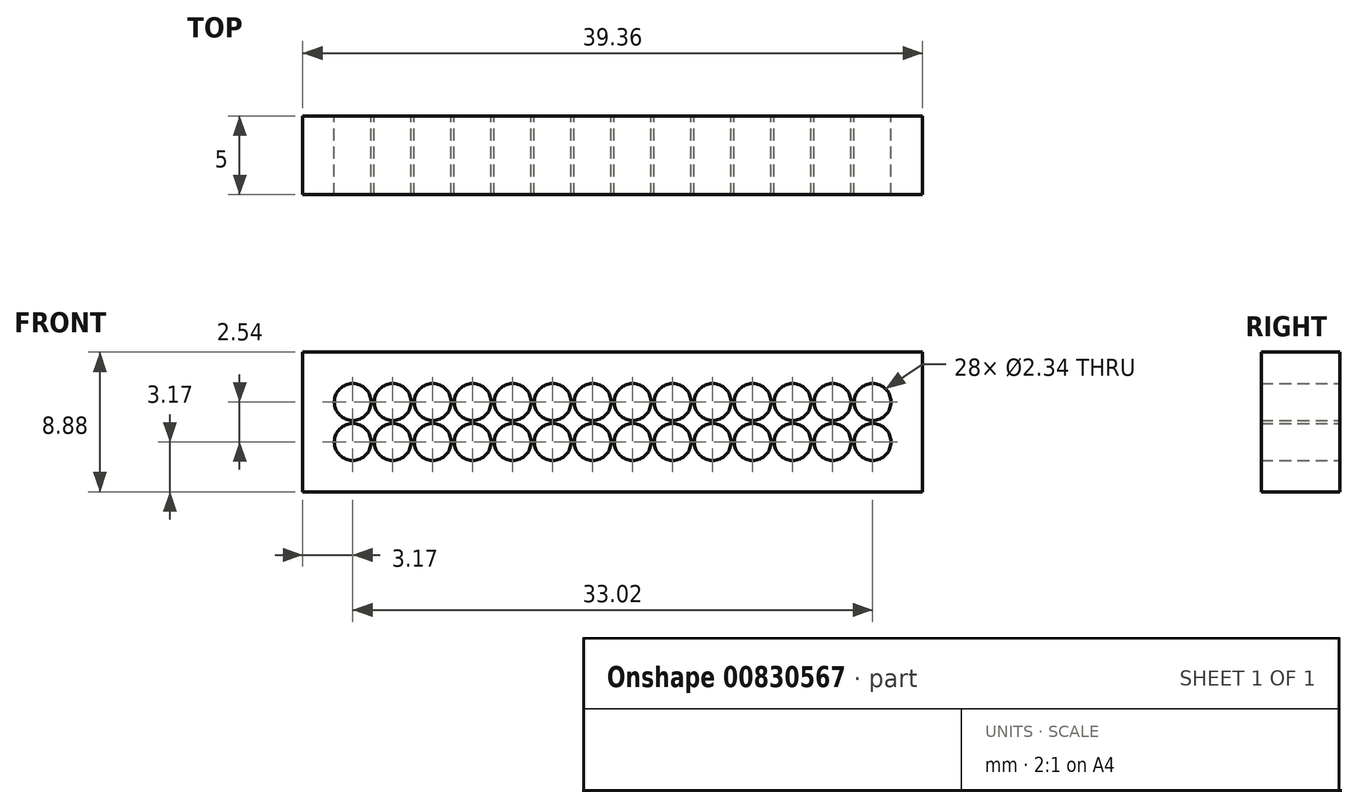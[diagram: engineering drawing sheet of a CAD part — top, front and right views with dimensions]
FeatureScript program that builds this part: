
annotation { "Feature Type Name" : "Feature", "Feature Type Description" : "" }
export const myFeature = defineFeature(function(context is Context, id is Id, definition is map)
    precondition{}
    {
        {
            var Q0;
            Q0=qCreatedBy(makeId("Front.planeOp"),FACE);
            var sketch = newSketch(context, id + "F0", { "sketchPlane" : qUnion([Q0])});
            skCircle(sketch, "E0", {"center": v(-1.27, 1.27) * mm, "radius": 1.17 * mm});
            skCircle(sketch, "E1", {"center": v(1.27, 1.27) * mm, "radius": 1.17 * mm});
            skCircle(sketch, "E2", {"center": v(-1.27, -1.27) * mm, "radius": 1.17 * mm});
            skCircle(sketch, "E3", {"center": v(1.27, -1.27) * mm, "radius": 1.17 * mm});
            skCircle(sketch, "E4", {"center": v(3.8, 1.27) * mm, "radius": 1.17 * mm});
            skCircle(sketch, "E5", {"center": v(6.35, 1.27) * mm, "radius": 1.17 * mm});
            skCircle(sketch, "E6", {"center": v(8.9, 1.27) * mm, "radius": 1.17 * mm});
            skCircle(sketch, "E7", {"center": v(11.43, 1.27) * mm, "radius": 1.17 * mm});
            skCircle(sketch, "E8", {"center": v(13.97, 1.27) * mm, "radius": 1.17 * mm});
            skCircle(sketch, "E9", {"center": v(16.51, 1.27) * mm, "radius": 1.17 * mm});
            skCircle(sketch, "E10", {"center": v(3.8, -1.27) * mm, "radius": 1.17 * mm});
            skCircle(sketch, "E11", {"center": v(6.35, -1.27) * mm, "radius": 1.17 * mm});
            skCircle(sketch, "E12", {"center": v(8.9, -1.27) * mm, "radius": 1.17 * mm});
            skCircle(sketch, "E13", {"center": v(11.43, -1.27) * mm, "radius": 1.17 * mm});
            skCircle(sketch, "E14", {"center": v(13.97, -1.27) * mm, "radius": 1.17 * mm});
            skCircle(sketch, "E15", {"center": v(16.51, -1.27) * mm, "radius": 1.17 * mm});
            skCircle(sketch, "E16", {"center": v(-3.8, 1.27) * mm, "radius": 1.17 * mm});
            skCircle(sketch, "E17", {"center": v(-6.35, 1.27) * mm, "radius": 1.17 * mm});
            skCircle(sketch, "E18", {"center": v(-8.9, 1.27) * mm, "radius": 1.17 * mm});
            skCircle(sketch, "E19", {"center": v(-11.43, 1.27) * mm, "radius": 1.17 * mm});
            skCircle(sketch, "E20", {"center": v(-13.97, 1.27) * mm, "radius": 1.17 * mm});
            skCircle(sketch, "E21", {"center": v(-16.51, 1.27) * mm, "radius": 1.17 * mm});
            skCircle(sketch, "E22", {"center": v(-3.8, -1.27) * mm, "radius": 1.17 * mm});
            skCircle(sketch, "E23", {"center": v(-6.35, -1.27) * mm, "radius": 1.17 * mm});
            skCircle(sketch, "E24", {"center": v(-8.9, -1.27) * mm, "radius": 1.17 * mm});
            skCircle(sketch, "E25", {"center": v(-11.43, -1.27) * mm, "radius": 1.17 * mm});
            skCircle(sketch, "E26", {"center": v(-13.97, -1.27) * mm, "radius": 1.17 * mm});
            skCircle(sketch, "E27", {"center": v(-16.51, -1.27) * mm, "radius": 1.17 * mm});
            skLineSegment(sketch, "E28.bottom", {"start": v(-19.68, 4.44) * mm, "end": v(19.68, 4.44) * mm});
            skLineSegment(sketch, "E28.top", {"start": v(-19.68, -4.44) * mm, "end": v(19.68, -4.44) * mm});
            skLineSegment(sketch, "E28.left", {"start": v(-19.68, 4.44) * mm, "end": v(-19.68, -4.44) * mm});
            skLineSegment(sketch, "E28.right", {"start": v(19.68, 4.44) * mm, "end": v(19.68, -4.44) * mm});
            skSolve(sketch);
        }
        {
            var Q0;
            Q0=makeQuery(id+"F0.imprint","IMPRINT",FACE,{"disambiguationData":[TD([[makeQuery(id+"F0.imprint","IMPRINT",EDGE,{"derivedFrom":sQuery(id+"F0.wireOp",EDGE,"E0")}),-1.0]])]});
            extrude(context, id + "F1", {"entities" : qUnion([Q0]), "depth" : 5 * mm, "offsetDistance" : 25 * mm});
        }
    });
